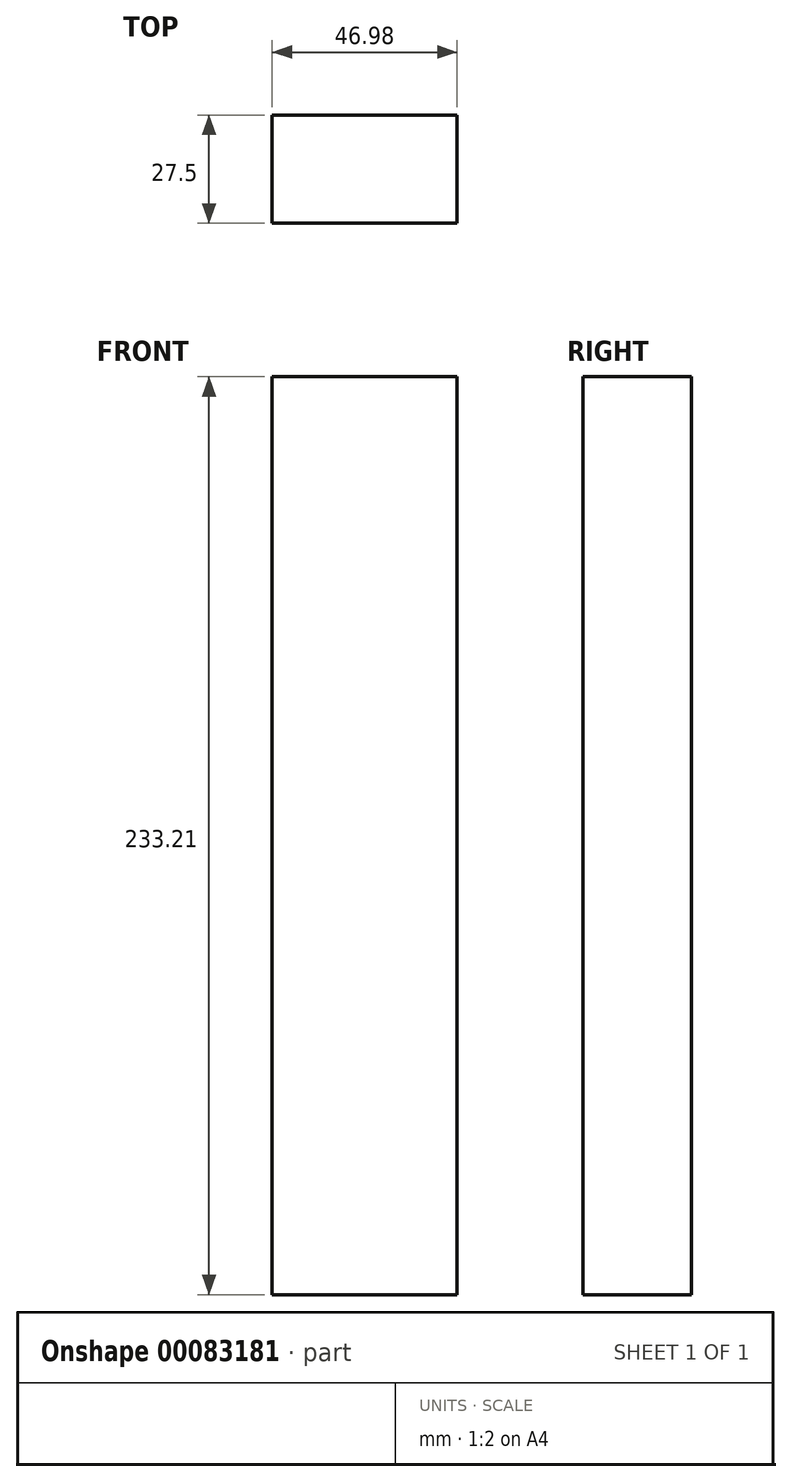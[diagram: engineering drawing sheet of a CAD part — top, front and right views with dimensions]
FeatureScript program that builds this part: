
annotation { "Feature Type Name" : "Feature", "Feature Type Description" : "" }
export const myFeature = defineFeature(function(context is Context, id is Id, definition is map)
    precondition{}
    {
        {
            var Q0;
            Q0=qCreatedBy(makeId("Top.planeOp"),FACE);
            var sketch = newSketch(context, id + "F0", { "sketchPlane" : qUnion([Q0])});
            skLineSegment(sketch, "E0.bottom", {"start": v(-233.75, 47.55) * mm, "end": v(-186.77, 47.55) * mm});
            skLineSegment(sketch, "E0.top", {"start": v(-233.75, 20.05) * mm, "end": v(-186.77, 20.05) * mm});
            skLineSegment(sketch, "E0.left", {"start": v(-233.75, 47.55) * mm, "end": v(-233.75, 20.05) * mm});
            skLineSegment(sketch, "E0.right", {"start": v(-186.77, 47.55) * mm, "end": v(-186.77, 20.05) * mm});
            skSolve(sketch);
        }
        {
            var Q0;
            Q0 = qSketchRegion(id + "F0", true);
            extrude(context, id + "F1", {"entities" : qUnion([Q0]), "depth" : 233.2 * mm});
        }
    });
